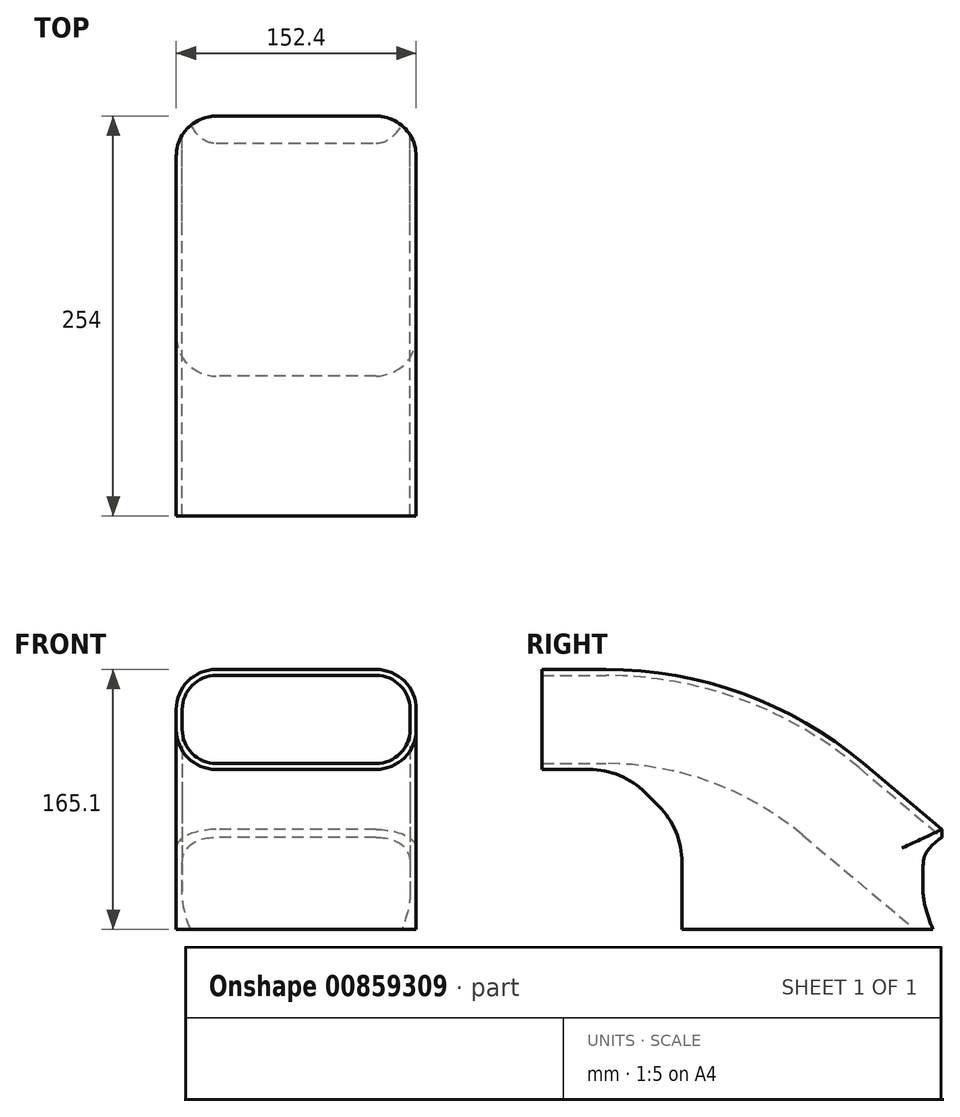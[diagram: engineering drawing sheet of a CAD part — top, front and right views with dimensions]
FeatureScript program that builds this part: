
annotation { "Feature Type Name" : "Feature", "Feature Type Description" : "" }
export const myFeature = defineFeature(function(context is Context, id is Id, definition is map)
    precondition{}
    {
        {
            var Q0;
            Q0=qCreatedBy(makeId("Right.planeOp"),FACE);
            var sketch = newSketch(context, id + "F0", { "sketchPlane" : qUnion([Q0])});
            skLineSegment(sketch, "E0", {"start": v(-254, 101.6) * mm, "end": v(0, 101.6) * mm, "construction": true});
            skLineSegment(sketch, "E1", {"start": v(0, 0) * mm, "end": v(-50.26, 42.18) * mm});
            skLineSegment(sketch, "E2", {"start": v(-213.53, 101.6) * mm, "end": v(-254, 101.6) * mm});
            skPoint(sketch, "E3.visualSharp", {"position": v(-94.95, 79.67) * mm});
            skLineSegment(sketch, "E4", {"start": v(-254, 101.6) * mm, "end": v(-254, 38.1) * mm});
            skLineSegment(sketch, "E5", {"start": v(-254, 38.1) * mm, "end": v(-224.24, 38.1) * mm});
            skLineSegment(sketch, "E6", {"start": v(-188.32, 23.22) * mm, "end": v(-179.98, 14.88) * mm});
            skPoint(sketch, "E7.visualSharp", {"position": v(-203.2, 38.1) * mm});
            skArc(sketch, "E7.filletArc", {"start": v(-188.32, 23.22) * mm, "mid": v(-204.8, 34.23) * mm, "end": v(-224.24, 38.1) * mm});
            skLineSegment(sketch, "E8", {"start": v(-165.1, -21.04) * mm, "end": v(-165.1, -63.5) * mm});
            skLineSegment(sketch, "E9", {"start": v(-165.1, -63.5) * mm, "end": v(0, -63.5) * mm});
            skLineSegment(sketch, "E10", {"start": v(0, -63.5) * mm, "end": v(0, 0) * mm});
            skPoint(sketch, "E11.visualSharp", {"position": v(-165.1, 0) * mm});
            skArc(sketch, "E11.filletArc", {"start": v(-165.1, -21.04) * mm, "mid": v(-168.97, -1.6) * mm, "end": v(-179.98, 14.88) * mm});
            skPoint(sketch, "E12.visualSharp", {"position": v(-121.08, 101.6) * mm});
            skArc(sketch, "E12.filletArc", {"start": v(-50.26, 42.18) * mm, "mid": v(-126.66, 86.28) * mm, "end": v(-213.53, 101.6) * mm});
            skSolve(sketch);
        }
        {
            var Q0;
            Q0 = qSketchRegion(id + "F0", true);
            extrude(context, id + "F1", {"entities" : qUnion([Q0]), "depth" : 152.4 * mm, "offsetDistance" : 25.4 * mm});
        }
        {
            var Q0;
            Q0=makeQuery(id+"F1.opExtrude","CAP_EDGE",EDGE,{"disambiguationData":[OSD([sQuery(id+"F0.wireOp",EDGE,"E2")])],"isStart":true});
            var Q1;
            Q1=makeQuery(id+"F1.opExtrude","CAP_EDGE",EDGE,{"disambiguationData":[OSD([sQuery(id+"F0.wireOp",EDGE,"E10")])],"isStart":true});
            var Q2;
            Q2=makeQuery(id+"F1.opExtrude","CAP_EDGE",EDGE,{"disambiguationData":[OSD([sQuery(id+"F0.wireOp",EDGE,"iiZaOJkz-wM9P-zI1z-V5Fo-HnQYC4dwPQ78")])],"isStart":true});
            fillet(context, id + "F2", {"entities" : qUnion([Q0, Q1, Q2]), "radius" : 25.4 * mm, "tangentPropagation" : true, "allowEdgeOverflow" : false});
        }
        {
            var Q0;
            Q0=makeQuery(id+"F1.opExtrude","CAP_EDGE",EDGE,{"disambiguationData":[OSD([sQuery(id+"F0.wireOp",EDGE,"E8")])],"isStart":true});
            fillet(context, id + "F3", {"entities" : qUnion([Q0]), "radius" : 25.4 * mm, "tangentPropagation" : true, "allowEdgeOverflow" : false});
        }
        {
            var Q0;
            Q0=makeQuery(id+"F1.opExtrude","CAP_EDGE",EDGE,{"disambiguationData":[OSD([sQuery(id+"F0.wireOp",EDGE,"E8")])],"isStart":false});
            fillet(context, id + "F4", {"entities" : qUnion([Q0]), "radius" : 25.4 * mm, "tangentPropagation" : true, "allowEdgeOverflow" : false});
        }
        {
            var Q0;
            Q0=makeQuery(id+"F1.opExtrude","CAP_EDGE",EDGE,{"disambiguationData":[OSD([sQuery(id+"F0.wireOp",EDGE,"E2")])],"isStart":false});
            var Q1;
            Q1=makeQuery(id+"F1.opExtrude","CAP_EDGE",EDGE,{"disambiguationData":[OSD([sQuery(id+"F0.wireOp",EDGE,"E10")])],"isStart":false});
            fillet(context, id + "F5", {"entities" : qUnion([Q0, Q1]), "radius" : 25.4 * mm, "tangentPropagation" : true, "allowEdgeOverflow" : false});
        }
        {
            var Q0;
            Q0=makeQuery(id+"F1.opExtrude","SWEPT_FACE",FACE,{"disambiguationData":[OSD([sQuery(id+"F0.wireOp",EDGE,"E4")])]});
            var sketch = newSketch(context, id + "F6", { "sketchPlane" : qUnion([Q0])});
            skArc(sketch, "E13.0", {"start": v(127, 41.91) * mm, "mid": v(142.27, 48.23) * mm, "end": v(148.6, 63.5) * mm});
            skLineSegment(sketch, "E13.1", {"start": v(25.4, 41.91) * mm, "end": v(127, 41.91) * mm});
            skLineSegment(sketch, "E13.2", {"start": v(148.6, 63.5) * mm, "end": v(148.6, 76.2) * mm});
            skArc(sketch, "E13.3", {"start": v(3.81, 63.5) * mm, "mid": v(10.13, 48.23) * mm, "end": v(25.4, 41.91) * mm});
            skArc(sketch, "E13.4", {"start": v(148.6, 76.2) * mm, "mid": v(142.27, 91.47) * mm, "end": v(127, 97.8) * mm});
            skLineSegment(sketch, "E13.5", {"start": v(127, 97.8) * mm, "end": v(25.4, 97.8) * mm});
            skArc(sketch, "E13.6", {"start": v(25.4, 97.8) * mm, "mid": v(10.13, 91.47) * mm, "end": v(3.81, 76.2) * mm});
            skLineSegment(sketch, "E13.7", {"start": v(3.81, 76.2) * mm, "end": v(3.81, 63.5) * mm});
            skSolve(sketch);
        }
        {
            var Q0;
            Q0=qCreatedBy(makeId("Right.planeOp"),FACE);
            cPlane(context, id + "F7", {"entities" : qUnion([Q0]), "cplaneType" : CPlaneType.OFFSET, "offset" : 76.2 * mm, "width" : 152.4 * mm, "height" : 152.4 * mm});
        }
        {
            var Q0;
            Q0=qCreatedBy(id+"F7.planeOp",FACE);
            var sketch = newSketch(context, id + "F8", { "sketchPlane" : qUnion([Q0])});
            skLineSegment(sketch, "E14.0", {"start": v(-70.67, 17.85) * mm, "end": v(74.68, -104.1) * mm});
            skArc(sketch, "E14.1", {"start": v(-213.53, 69.85) * mm, "mid": v(-137.52, 56.45) * mm, "end": v(-70.67, 17.85) * mm});
            skLineSegment(sketch, "E14.2", {"start": v(-254, 69.85) * mm, "end": v(-213.53, 69.85) * mm});
            skSolve(sketch);
        }
        {
            var Q0;
            Q0=makeQuery(id+"F6.imprint","IMPRINT",FACE,{"disambiguationData":[TD([[makeQuery(id+"F6.imprint","IMPRINT",EDGE,{"derivedFrom":sQuery(id+"F6.wireOp",EDGE,"E13.0")}),1.0]])]});
            var Q1;
            Q1=sQuery(id+"F8.wireOp",EDGE,"E14.2");
            var Q2;
            Q2=sQuery(id+"F8.wireOp",EDGE,"E14.1");
            var Q3;
            Q3=sQuery(id+"F8.wireOp",EDGE,"E14.0");
            sweep(context, id + "F9", {"operationType" : NewBodyOperationType.REMOVE, "profiles" : qUnion([Q0]), "path" : qUnion([Q1, Q2, Q3])});
        }
    });
